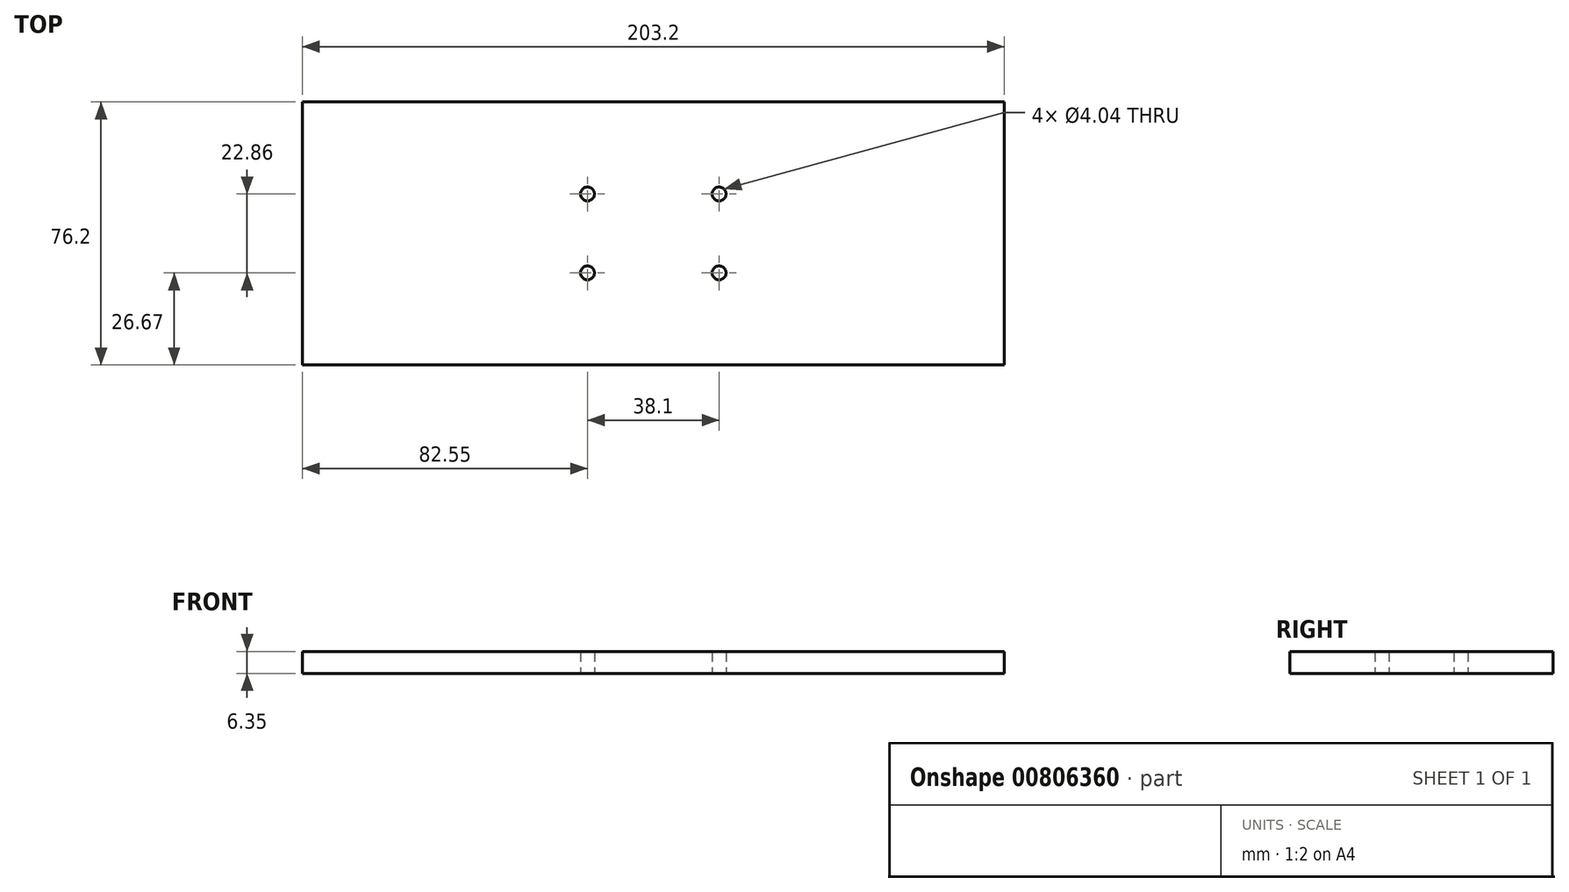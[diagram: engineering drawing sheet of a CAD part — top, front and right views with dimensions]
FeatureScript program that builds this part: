
annotation { "Feature Type Name" : "Feature", "Feature Type Description" : "" }
export const myFeature = defineFeature(function(context is Context, id is Id, definition is map)
    precondition{}
    {
        {
            var Q0;
            Q0=qCreatedBy(makeId("Top.planeOp"),FACE);
            var sketch = newSketch(context, id + "F0", { "sketchPlane" : qUnion([Q0])});
            skLineSegment(sketch, "E0.bottom", {"start": v(101.6, 38.1) * mm, "end": v(-101.6, 38.1) * mm});
            skLineSegment(sketch, "E0.top", {"start": v(101.6, -38.1) * mm, "end": v(-101.6, -38.1) * mm});
            skLineSegment(sketch, "E0.left", {"start": v(101.6, 38.1) * mm, "end": v(101.6, -38.1) * mm});
            skLineSegment(sketch, "E0.right", {"start": v(-101.6, 38.1) * mm, "end": v(-101.6, -38.1) * mm});
            skPoint(sketch, "E0.middle", {"position": v(0, 0) * mm});
            skLineSegment(sketch, "E1.bottom", {"start": v(31.75, 19.05) * mm, "end": v(-31.75, 19.05) * mm});
            skLineSegment(sketch, "E1.top", {"start": v(31.75, -19.05) * mm, "end": v(-31.75, -19.05) * mm});
            skLineSegment(sketch, "E1.left", {"start": v(31.75, 19.05) * mm, "end": v(31.75, -19.05) * mm});
            skLineSegment(sketch, "E1.right", {"start": v(-31.75, 19.05) * mm, "end": v(-31.75, -19.05) * mm});
            skCircle(sketch, "E2", {"center": v(-19.05, 11.43) * mm, "radius": 2.02 * mm});
            skCircle(sketch, "E3", {"center": v(-19.05, -11.43) * mm, "radius": 2.02 * mm});
            skCircle(sketch, "E4", {"center": v(19.05, 11.43) * mm, "radius": 2.02 * mm});
            skCircle(sketch, "E5", {"center": v(19.05, -11.43) * mm, "radius": 2.02 * mm});
            skSolve(sketch);
        }
        {
            var Q0;
            Q0 = qSketchRegion(id + "F0", true);
            var Q1;
            Q1=makeQuery(id+"F0.imprint","IMPRINT",FACE,{"disambiguationData":[TD([[makeQuery(id+"F0.imprint","IMPRINT",EDGE,{"derivedFrom":sQuery(id+"F0.wireOp",EDGE,"E1.bottom")}),1.0]])]});
            extrude(context, id + "F1", {"entities" : qUnion([Q0, Q1]), "depth" : 6.35 * mm, "offsetDistance" : 25.4 * mm});
        }
    });
